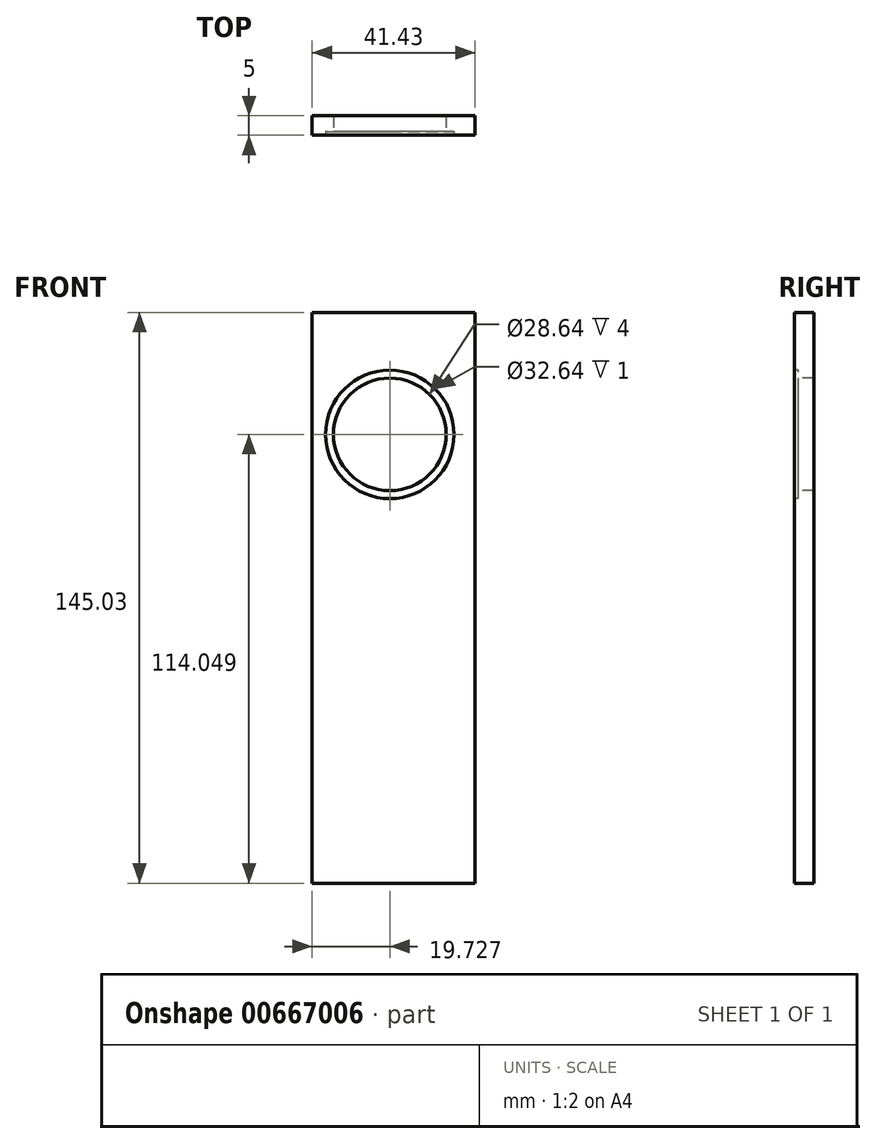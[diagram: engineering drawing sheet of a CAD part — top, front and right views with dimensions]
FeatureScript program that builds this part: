
annotation { "Feature Type Name" : "Feature", "Feature Type Description" : "" }
export const myFeature = defineFeature(function(context is Context, id is Id, definition is map)
    precondition{}
    {
        {
            var Q0;
            Q0=qCreatedBy(makeId("Front.planeOp"),FACE);
            var sketch = newSketch(context, id + "F0", { "sketchPlane" : qUnion([Q0])});
            skLineSegment(sketch, "E0.bottom", {"start": v(-90.6, -80.76) * mm, "end": v(-49.17, -80.76) * mm});
            skLineSegment(sketch, "E0.top", {"start": v(-90.6, 64.27) * mm, "end": v(-49.17, 64.27) * mm});
            skLineSegment(sketch, "E0.left", {"start": v(-90.6, -80.76) * mm, "end": v(-90.6, 64.27) * mm});
            skLineSegment(sketch, "E0.right", {"start": v(-49.17, -80.76) * mm, "end": v(-49.17, 64.27) * mm});
            skSolve(sketch);
        }
        {
            var Q0;
            Q0=makeQuery(id+"F0.imprint","IMPRINT",FACE,{"disambiguationData":[TD([[makeQuery(id+"F0.imprint","IMPRINT",EDGE,{"derivedFrom":sQuery(id+"F0.wireOp",EDGE,"E0.bottom")}),1.0]])]});
            extrude(context, id + "F1", {"entities" : qUnion([Q0]), "depth" : 5 * mm, "offsetDistance" : 25 * mm});
        }
        {
            var Q0;
            Q0=makeQuery(id+"F1.opExtrude","CAP_FACE",FACE,{"disambiguationData":[OSD([sQuery(id+"F0.wireOp",EDGE,"E0.bottom"),sQuery(id+"F0.wireOp",EDGE,"E0.top"),sQuery(id+"F0.wireOp",EDGE,"E0.left"),sQuery(id+"F0.wireOp",EDGE,"E0.right")])],"isStart":false});
            var sketch = newSketch(context, id + "F2", { "sketchPlane" : qUnion([Q0])});
            skCircle(sketch, "E1", {"center": v(-70.87, 33.29) * mm, "radius": 16.32 * mm});
            skCircle(sketch, "E2", {"center": v(-70.87, 33.29) * mm, "radius": 14.32 * mm});
            skSolve(sketch);
        }
        {
            var Q0;
            Q0=makeQuery(id+"F2.imprint","IMPRINT",FACE,{"disambiguationData":[TD([[makeQuery(id+"F2.imprint","IMPRINT",EDGE,{"derivedFrom":sQuery(id+"F2.wireOp",EDGE,"E1")}),-1.0]])]});
            var sketch = newSketch(context, id + "F3", { "sketchPlane" : qUnion([Q0])});
            skCircle(sketch, "E3", {"center": v(-71.02, 33.22) * mm, "radius": 16.63 * mm});
            skSolve(sketch);
        }
        {
            var Q0;
            Q0=makeQuery(id+"F2.imprint","IMPRINT",FACE,{"disambiguationData":[TD([[makeQuery(id+"F2.imprint","IMPRINT",EDGE,{"derivedFrom":sQuery(id+"F2.wireOp",EDGE,"E2")}),1.0]])]});
            extrude(context, id + "F4", {"entities" : qUnion([Q0]), "operationType" : NewBodyOperationType.REMOVE, "oppositeDirection" : true, "depth" : 5 * mm, "offsetDistance" : 25 * mm});
        }
        {
            var Q0;
            Q0=makeQuery(id+"F3.imprint","IMPRINT",FACE,{"disambiguationData":[TD([[makeQuery(id+"F3.imprint","IMPRINT",EDGE,{"derivedFrom":makeQuery(id+"F2.imprint","IMPRINT",EDGE,{"derivedFrom":sQuery(id+"F2.wireOp",EDGE,"E1")})}),1.0]])]});
            extrude(context, id + "F5", {"entities" : qUnion([Q0]), "operationType" : NewBodyOperationType.REMOVE, "oppositeDirection" : true, "depth" : 1 * mm, "offsetDistance" : 25 * mm});
        }
    });
